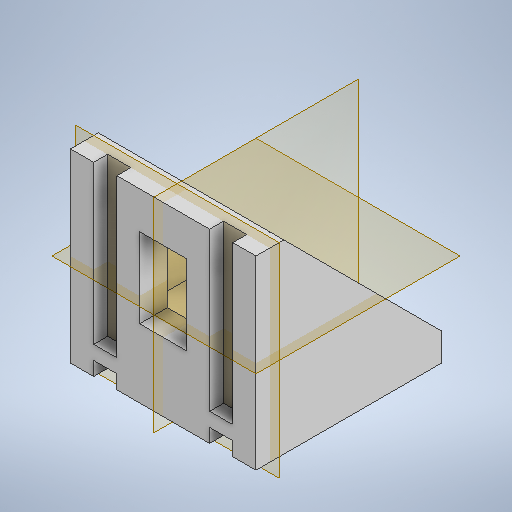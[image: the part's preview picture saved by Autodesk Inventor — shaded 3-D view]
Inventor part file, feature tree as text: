
AUTODESK INVENTOR PART (.ipt)
format: ipt  version: 2025.2 (Build 292293000, 293)  size: 313,856 bytes
history: native  units: mm
features: extrude x5, sketch x5, other x1, mirror x1
ambient origin geometry x8: Origin, YZ Plane, XZ Plane, XY Plane, X Axis, Y Axis, Z Axis, Center Point
bodies: Body1 (feature_tree)
feature tree (12):
  other  "Sólido1"
  extrude  "Extrusión1"  Depth=4.0mm
  extrude  "Extrusión2"  Depth=8.6mm
  extrude  "Extrusión3"  Depth=2.5mm
  extrude  "Extrusión4"  Depth=1.5mm TaperAngle=0.0deg
  extrude  "Extrusión5"  Depth=4.0mm
  mirror  "Simetría1"
  sketch  "Boceto1"  dims[d0=20.0mm d1=4.0mm]
  sketch  "Boceto2"  dims[d2=5.1mm d3=8.6mm]
  sketch  "Boceto5"  dims[d4=3.0mm d5=0.0mm d6=2.5mm]
  sketch  "Boceto6"  dims[d7=5.0mm d8=1.5mm d9=0.0mm]
  sketch  "Boceto7"  dims[d12=20.0mm d14=5.0mm d15=8.5mm d16=4.0mm d17=3.0mm d18=0.0mm d19=2.5mm d20=5.0mm d23=1.5mm d24=0.0mm d25=1.5mm d26=0.0mm]
